FCSTD DOCUMENT  (FreeCAD 0.20R29410 (Git))
Label: grip
License: All rights reserved
LicenseURL: http://en.wikipedia.org/wiki/All_rights_reserved
objects: Sketcher::SketchObject×1
note: 1 computed .brp shape members not serialized (recipe doc carries the construction recipe); baked Part::Feature solids carry a one-line shape summary decoded from their .brp

FEATURE [Sketcher::SketchObject] Sketch
  FullyConstrained = false
  sketch-geometry (22):
    g0: LineSegment StartX=0 StartY=0 StartZ=0 EndX=7.5 EndY=0 EndZ=0
    g1: LineSegment StartX=7.5 StartY=0 StartZ=0 EndX=37.685 EndY=29.9185 EndZ=0
    g2: LineSegment StartX=37.685 StartY=29.9185 StartZ=0 EndX=37.685 EndY=48.7085 EndZ=0
    g3: LineSegment StartX=37.685 StartY=48.7085 StartZ=0 EndX=29.9866 EndY=56.3233 EndZ=0
    g4: LineSegment StartX=29.9866 StartY=56.3233 StartZ=0 EndX=29.9866 EndY=66.5833 EndZ=0
    g5: LineSegment StartX=29.9866 StartY=66.5833 StartZ=0 EndX=44.2057 EndY=52.5185 EndZ=0
    g6: LineSegment StartX=44.2057 StartY=52.5185 StartZ=0 EndX=44.2057 EndY=17.5185 EndZ=0
    g7: LineSegment StartX=44.2057 StartY=17.5185 StartZ=0 EndX=14.0207 EndY=-12.4 EndZ=0
    g8: LineSegment StartX=14.0207 StartY=-12.4 StartZ=0 EndX=0 EndY=-12.4 EndZ=0
    g9: LineSegment StartX=7.5 StartY=0 StartZ=0 EndX=14.0207 EndY=-12.4 EndZ=0
    g10: LineSegment StartX=37.685 StartY=29.9185 StartZ=0 EndX=44.2057 EndY=17.5185 EndZ=0
    g11: LineSegment StartX=0 StartY=0 StartZ=0 EndX=-7.5 EndY=0 EndZ=0
    g12: LineSegment StartX=0 StartY=-12.4 StartZ=0 EndX=-14.0207 EndY=-12.4 EndZ=0
    g13: LineSegment StartX=-7.5 StartY=0 StartZ=0 EndX=-14.0207 EndY=-12.4 EndZ=0
    g14: LineSegment StartX=-7.5 StartY=0 StartZ=0 EndX=-37.685 EndY=29.9185 EndZ=0
    g15: LineSegment StartX=-37.685 StartY=29.9185 StartZ=0 EndX=-44.2057 EndY=17.5185 EndZ=0
    g16: LineSegment StartX=-44.2057 StartY=17.5185 StartZ=0 EndX=-14.0207 EndY=-12.4 EndZ=0
    g17: LineSegment StartX=-44.2057 StartY=17.5185 StartZ=0 EndX=-44.2057 EndY=52.5185 EndZ=0
    g18: LineSegment StartX=-44.2057 StartY=52.5185 StartZ=0 EndX=-29.9866 EndY=66.5833 EndZ=0
    g19: LineSegment StartX=-29.9866 StartY=66.5833 StartZ=0 EndX=-29.9866 EndY=56.3233 EndZ=0
    g20: LineSegment StartX=-29.9866 StartY=56.3233 StartZ=0 EndX=-37.685 EndY=48.7085 EndZ=0
    g21: LineSegment StartX=-37.685 StartY=48.7085 StartZ=0 EndX=-37.685 EndY=29.9185 EndZ=0
  constraints (60):
    c: Coincident(g0,g-1)
    c: PointOnObject(g0,g-1)
    c: Coincident(g2,g1)
    c: Vertical(g2)
    c: Coincident(g3,g2)
    c: Coincident(g4,g3)
    c: Vertical(g4)
    c: Coincident(g6,g5)
    c: Vertical(g6)
    c: Coincident(g8,g7)
    c: PointOnObject(g8,g-2)
    c: Horizontal(g8)
    c: Coincident(g7,g6)
    c: Coincident(g5,g4)
    c: Parallel(g3,g5)
    c: Parallel(g1,g7)
    c: Coincident(g0,g1)
    c: Distance(g5) = 20
    c: Distance(g6) = 35
    c: Distance(g7) = 42.5
    c: Distance(g0) = 7.5
    c: Coincident(g9,g0)
    c: Coincident(g9,g7)
    c: Coincident(g10,g1)
    c: Coincident(g10,g6)
    c: Parallel(g10,g9)
    c: DistanceY(g8,g0) = 12.4
    c: Distance(g2) = 18.79
    c: Distance(g9) = 14.01
    c: DistanceY(g4,g4) = 10.26
    c: Coincident(g11,g0)
    c: PointOnObject(g11,g-1)
    c: Coincident(g12,g8)
    c: Horizontal(g12)
    c: Coincident(g13,g11)
    c: Coincident(g13,g12)
    c: Coincident(g14,g11)
    c: Coincident(g16,g12)
    c: Coincident(g17,g15)
    c: Vertical(g17)
    c: Coincident(g19,g18)
    c: Vertical(g19)
    c: Coincident(g20,g19)
    c: Coincident(g21,g14)
    c: Coincident(g17,g18)
    c: Coincident(g16,g15)
    c: Coincident(g21,g20)
    c: Coincident(g14,g15)
    c: Equal(g21,g2)
    c: Equal(g19,g4)
    c: Equal(g18,g5)
    c: Equal(g17,g6)
    c: Equal(g13,g9)
    c: Equal(g11,g0)
    c: Equal(g16,g7)
    c: Equal(g14,g1)
    c: Equal(g15,g10)
    c: Equal(g3,g20)
    c: Vertical(g21)
    c: Horizontal(g18,g4)
